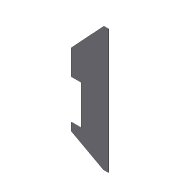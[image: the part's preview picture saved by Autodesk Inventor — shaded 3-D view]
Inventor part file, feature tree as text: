
AUTODESK INVENTOR PART (.ipt)
format: ipt  version: 2012 (Build 160160000, 160)  size: 94,208 bytes
history: native  units: in
note: dims shown in document units (in); Inventor stores cm internally (conversion verified against a paired STEP export)
features: extrude x3, sketch x3
ambient origin geometry x8: Origin, YZ Plane, XZ Plane, XY Plane, X Axis, Y Axis, Z Axis, Center Point
bodies: Solid1 (feature_tree)
feature tree (6):
  extrude  "Extrusion1"  Depth=25.0in
  extrude  "Extrusion2"  Depth=3.5in
  extrude  "Extrusion4"  Depth=7.0in
  sketch  "Sketch1"  dims[d0=7.5in d1=25.0in]
  sketch  "Sketch2"  dims[d2=0.125in d3=0.0in d5=3.5in]
  sketch  "Sketch4"  dims[d6=0.125in d7=0.0in d8=7.0in d9=1.0in d17=8.0in d18=2.0in d19=1.0in d20=0.0in d21=5.0in]
